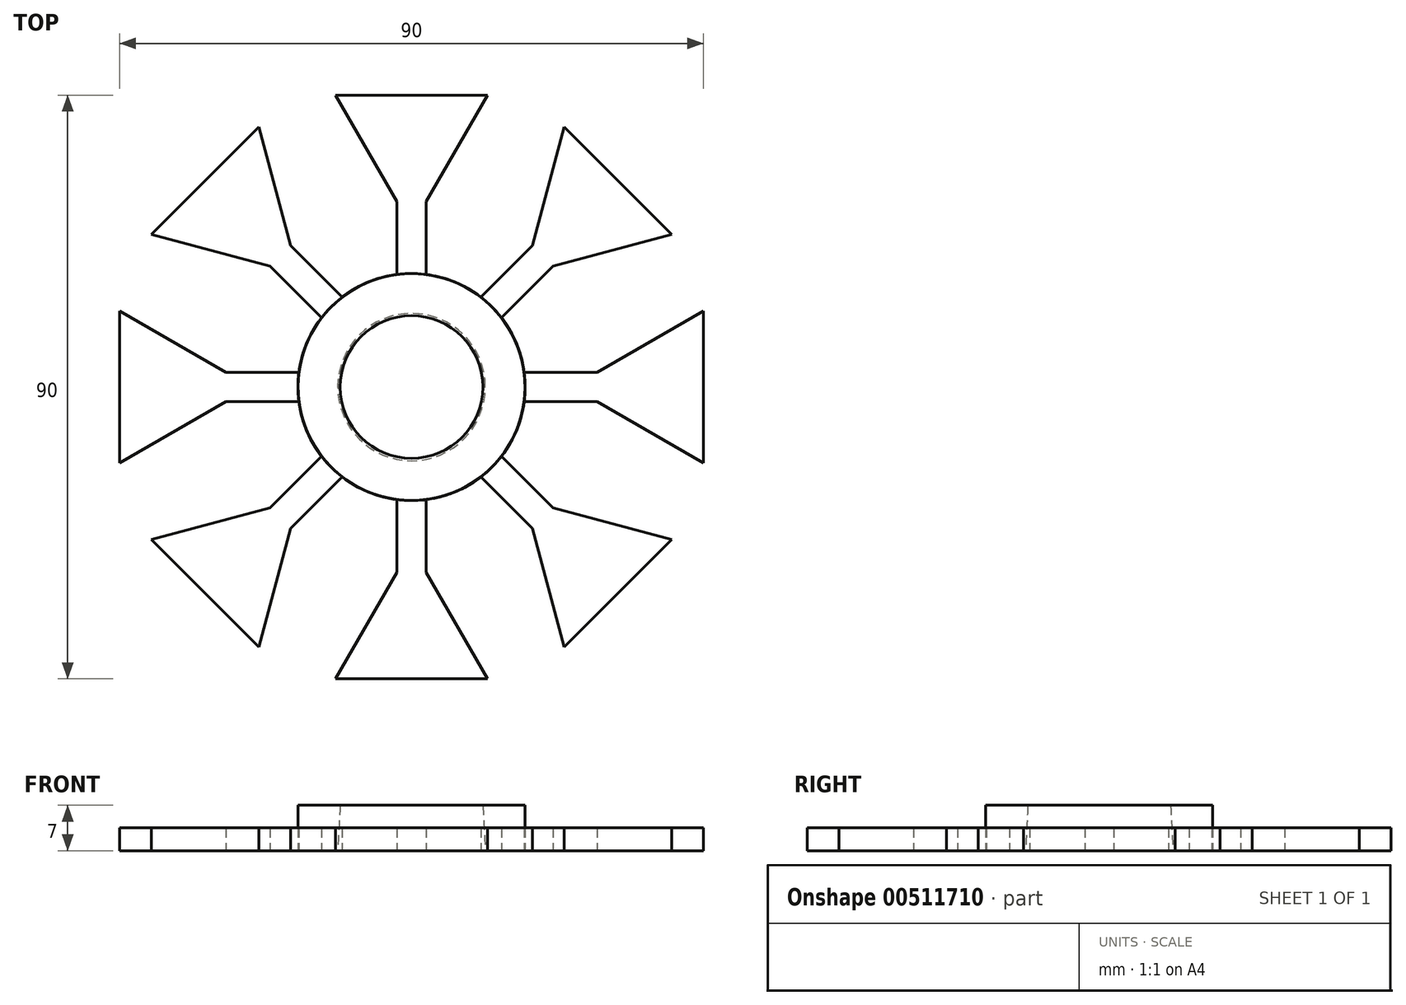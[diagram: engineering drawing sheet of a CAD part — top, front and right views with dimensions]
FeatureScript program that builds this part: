
annotation { "Feature Type Name" : "Feature", "Feature Type Description" : "" }
export const myFeature = defineFeature(function(context is Context, id is Id, definition is map)
    precondition{}
    {
        {
            var Q0;
            Q0=qCreatedBy(makeId("Top.planeOp"),FACE);
            var sketch = newSketch(context, id + "F0", { "sketchPlane" : qUnion([Q0])});
            skCircle(sketch, "E0", {"center": v(0, 0) * mm, "radius": 17.5 * mm});
            skSolve(sketch);
        }
        {
            var Q0;
            Q0=makeQuery(id+"F0.imprint","IMPRINT",FACE,{"disambiguationData":[TD([[makeQuery(id+"F0.imprint","IMPRINT",EDGE,{"derivedFrom":sQuery(id+"F0.wireOp",EDGE,"E0")}),1.0]])]});
            extrude(context, id + "F1", {"entities" : qUnion([Q0]), "depth" : 7 * mm});
        }
        {
            var Q0;
            Q0=makeQuery(id+"F1.opExtrude","CAP_FACE",FACE,{"disambiguationData":[OSD([sQuery(id+"F0.wireOp",EDGE,"E0")])],"isStart":false});
            var sketch = newSketch(context, id + "F2", { "sketchPlane" : qUnion([Q0])});
            skCircle(sketch, "E1", {"center": v(0, 0) * mm, "radius": 11 * mm});
            skSolve(sketch);
        }
        {
            var Q0;
            Q0=makeQuery(id+"F2.imprint","IMPRINT",FACE,{"disambiguationData":[TD([[makeQuery(id+"F2.imprint","IMPRINT",EDGE,{"derivedFrom":sQuery(id+"F2.wireOp",EDGE,"E1")}),1.0]])]});
            extrude(context, id + "F3", {"entities" : qUnion([Q0]), "operationType" : NewBodyOperationType.REMOVE, "endBound" : BoundingType.THROUGH_ALL, "oppositeDirection" : true, "depth" : 7 * mm, "hasDraft" : true, "draftAngle" : 3 * degree});
        }
        {
            var Q0;
            Q0=qCreatedBy(makeId("Top.planeOp"),FACE);
            var sketch = newSketch(context, id + "F4", { "sketchPlane" : qUnion([Q0])});
            skLineSegment(sketch, "E2.bottom", {"start": v(2.24, -34.24) * mm, "end": v(-2.24, -34.24) * mm});
            skLineSegment(sketch, "E2.top", {"start": v(2.24, -17.01) * mm, "end": v(-2.24, -17.01) * mm});
            skLineSegment(sketch, "E2.left", {"start": v(2.24, -34.24) * mm, "end": v(2.24, -17.01) * mm});
            skLineSegment(sketch, "E2.right", {"start": v(-2.24, -34.24) * mm, "end": v(-2.24, -17.01) * mm});
            skPoint(sketch, "E2.middle", {"position": v(0, -25.62) * mm});
            skSolve(sketch);
        }
        {
            var Q0;
            Q0=qCreatedBy(makeId("Top.planeOp"),FACE);
            var sketch = newSketch(context, id + "F5", { "sketchPlane" : qUnion([Q0])});
            skCircle(sketch, "E3.cCircle", {"center": v(0, -39.85) * mm, "radius": 5.2 * mm, "construction": true});
            skLineSegment(sketch, "E3.0", {"start": v(3, -45.05) * mm, "end": v(-3, -45.05) * mm});
            skLineSegment(sketch, "E3.1", {"start": v(-3, -45.05) * mm, "end": v(-6.01, -39.85) * mm});
            skLineSegment(sketch, "E3.2", {"start": v(-6.01, -39.85) * mm, "end": v(-3, -34.64) * mm});
            skLineSegment(sketch, "E3.3", {"start": v(-3, -34.64) * mm, "end": v(3, -34.64) * mm});
            skLineSegment(sketch, "E3.4", {"start": v(3, -34.64) * mm, "end": v(6.01, -39.85) * mm});
            skLineSegment(sketch, "E3.5", {"start": v(6.01, -39.85) * mm, "end": v(3, -45.05) * mm});
            skPoint(sketch, "E3.0.midPoint", {"position": v(0, -45.05) * mm});
            skSolve(sketch);
        }
        {
            var Q0;
            Q0=makeQuery(id+"F5.imprint","IMPRINT",FACE,{"disambiguationData":[TD([[makeQuery(id+"F5.imprint","IMPRINT",EDGE,{"derivedFrom":sQuery(id+"F5.wireOp",EDGE,"E3.0")}),-1.0]])]});
            var Q1;
            Q1=makeQuery(id+"F4.imprint","IMPRINT",FACE,{"disambiguationData":[TD([[makeQuery(id+"F4.imprint","IMPRINT",EDGE,{"derivedFrom":sQuery(id+"F4.wireOp",EDGE,"E2.bottom")}),-1.0]])]});
            extrude(context, id + "F6", {"entities" : qUnion([Q0, Q1]), "operationType" : NewBodyOperationType.ADD, "depth" : 3.5 * mm});
        }
        {
            var Q0;
            Q0=makeQuery(id+"F6.opExtrude","SWEPT_BODY",BODY,{"disambiguationData":[OSD([sQuery(id+"F5.wireOp",EDGE,"E3.0"),sQuery(id+"F5.wireOp",EDGE,"E3.1"),sQuery(id+"F5.wireOp",EDGE,"E3.2"),sQuery(id+"F5.wireOp",EDGE,"E3.3"),sQuery(id+"F5.wireOp",EDGE,"E3.4"),sQuery(id+"F5.wireOp",EDGE,"E3.5")])]});
            deleteBodies(context, id + "F7", {"entities" : qUnion([Q0])});
        }
        {
            var Q0;
            Q0=qCreatedBy(makeId("Top.planeOp"),FACE);
            var sketch = newSketch(context, id + "F8", { "sketchPlane" : qUnion([Q0])});
            skCircle(sketch, "E4.cCircle", {"center": v(0, -38.24) * mm, "radius": 6.76 * mm, "construction": true});
            skLineSegment(sketch, "E4.0", {"start": v(11.7, -45) * mm, "end": v(-11.7, -45) * mm});
            skLineSegment(sketch, "E4.1", {"start": v(-11.7, -45) * mm, "end": v(0, -24.73) * mm});
            skLineSegment(sketch, "E4.2", {"start": v(0, -24.73) * mm, "end": v(11.7, -45) * mm});
            skPoint(sketch, "E4.0.midPoint", {"position": v(0, -45) * mm});
            skSolve(sketch);
        }
        {
            var Q0;
            Q0=makeQuery(id+"F8.imprint","IMPRINT",FACE,{"disambiguationData":[TD([[makeQuery(id+"F8.imprint","IMPRINT",EDGE,{"derivedFrom":sQuery(id+"F8.wireOp",EDGE,"E4.0")}),-1.0]])]});
            extrude(context, id + "F9", {"entities" : qUnion([Q0]), "operationType" : NewBodyOperationType.ADD, "depth" : 3.5 * mm});
        }
        {
            var Q0;
            Q0=makeQuery(id+"F1.opExtrude","SWEPT_BODY",BODY,{"disambiguationData":[OSD([sQuery(id+"F0.wireOp",EDGE,"E0")])]});
            var Q1;
            Q1=makeQuery(id+"F1.opExtrude","SWEPT_FACE",FACE,{"disambiguationData":[OSD([sQuery(id+"F0.wireOp",EDGE,"E0")])]});
            circularPattern(context, id + "F10", {"entities" : qUnion([Q0]), "axis" : qUnion([Q1]), "angle" : 360 * degree, "instanceCount" : 8, "equalSpace" : true});
        }
    });
